# Revit family: Gira_123927
name_source: partatom
category: Electrical Fixtures
revit_build: Autodesk Revit 2017 (Build: 20160225_1515(x64)
units: mm (PartAtom-declared; Revit-internal decimal feet)

## family parameters
Cut with Voids When Loaded = No
Host = Face
Maintain Annotation Orientation = No
Part Type = Normal
Room Calculation Point = No
Round Connector Dimension = Use Diameter
Shared = No

## types (1)
- SM video home st. Plus System 55 p.white m
    Add-on device = No
    Automatic door opener = Yes
    Available = No
    BIM (1) = https://media.stage.bim.site
    Can be connected to smartphone = No
    Category = Indoor station door communication
    Colour = White
    Control extra function(s) = Yes
    Data sheet (1) = https://katalog.gira.de
    Default Elevation = 1219 mm
    Description = SM video home st.Plus Sys55 PWm,Surface-mounted video home station Plus,System 55,pure white matt,Features:,- When using an additional power supply for door communication, up to 28 surface-mounted home stations video can be used in parallel.,- The Video AP Plus home station video automatically detects whether a power supply for door communication is connected. A jumper between the additional power supply and bus is not required.,- Colour display with LED backlighting.,- OSD function, i.e. text presentation in display for status display and menu guidance.,- Capacitive operating buttons with integrated LEDs for status display: the buttons are operated with a light touch.,- Connectable automatic door opener: when this function is activated, the door opener is automatically operated after pressing the door station call button.,- Automatic call acceptance: direct speaking or listening into a room following an internal call.,- Toll-free in-house intercom communication with up to ten other home stations.,The operating buttons of the Video AP Plus control the following functions::,- Manual switching on off of TFT colour display.,- Camera changeover - specific selection of connected colour cameras. Text in the display indicates which camera is currently being controlled.,- Switching light and other functions in conjunction with the switching actuator or the flush-mounted switching actuator.,- Control of the door opener.,- Switching the ringtone on and off.,- Call acceptance.,- Activation of the enforcement function.,- Adjustment of ring tone and voice volume.,Functions in the end customer menu::,- Internal call, switching action, ringtone melody, brightness, colour intensity, contrast, switch-on time of the display, language (21 languages can be selected), button tones, automatic door opener (when enabled by the installer), automatic call acceptance (when enabled by the installer).,Additional functions in the installer menu::,- Selection of main secondary display, frequency setting, termination of the cable, version indication, factory setting, switching display on off, switching LED illumination on off, call button assignment, internal call assignment, enabling of automatic door opener and automatic call acceptance.,- Card slot for SD memory card.,- SD memory card.,New additional functions in the end customer menu::,- Internal image memory (when enabled by the installer) for up to 48 images. Manual transfer from internal to external image memory (SD memory card). Manual deletion of image memory. Manual triggering of snapshot. Rename switching actions and internal calls. Change date time.,New additional functions in the installer menu::,- Release of the internal image memory. Set the image interval and recording speed. Set date time.,Properties of the SD memory card::,- Directory for ten ringing tones, five of which can be configured freely in WAVE format. Folder for external image memory (max. 200 images).,,Notes :,- Installation is possible either without a frame or with a 2-gang frame without crossbar from the System 55, Gira F100, or Gira E22 design lines.
    Function lamps = Yes
    GTIN = 4010337016243
    HAN = 123927
    Hearing aid compatible = No
    HeinzeBIM = https://bimportal.heinze.de
    Installation technique = Bus system
    Internal communication = Yes
    Loudness control = Yes
    Manufacturer = Gira
    Manufacturer URL = https://www.gira.de
    Material = Other
    Mounting method = Surface mounted (plaster)
    Mutable call tone = Yes
    Name = SM video home st. Plus System 55 p.white m
    Operation door lock = Yes
    Overhear protected = Yes
    Picture system = PAL
    Specific call tone = Yes
    URL = http://katalog.gira.de
    With memory function = No
    With touch screen = No
    With video = Yes

## geometry (parser evidence)
native form markers: Sweep x2
no freeform markers — native parametric forms only
